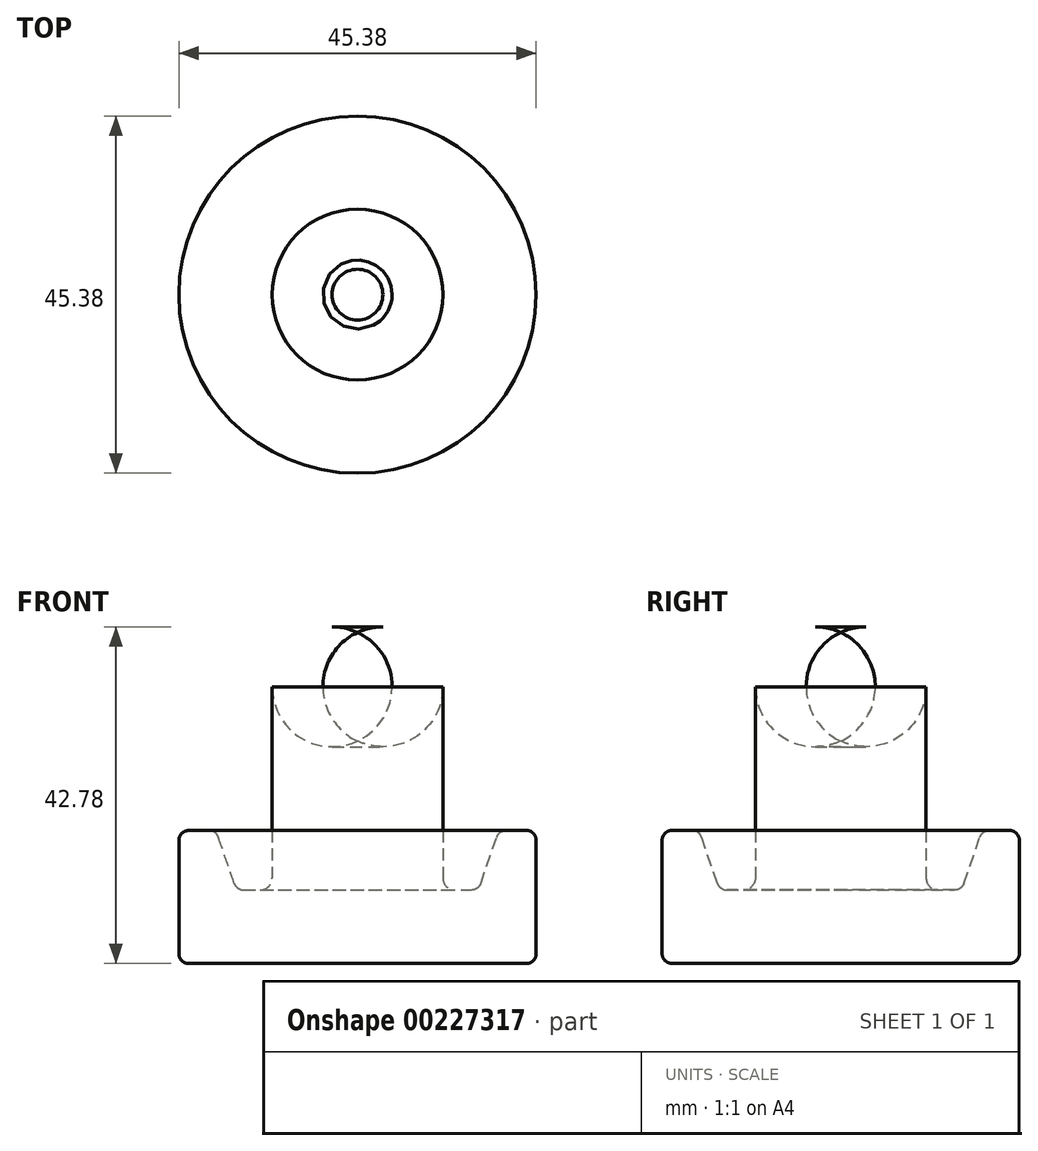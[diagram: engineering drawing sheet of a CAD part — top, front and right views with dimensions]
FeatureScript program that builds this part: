
annotation { "Feature Type Name" : "Feature", "Feature Type Description" : "" }
export const myFeature = defineFeature(function(context is Context, id is Id, definition is map)
    precondition{}
    {
        {
            var Q0;
            Q0=qCreatedBy(makeId("Right.planeOp"),FACE);
            var sketch = newSketch(context, id + "F0", { "sketchPlane" : qUnion([Q0])});
            skLineSegment(sketch, "E0", {"start": v(0, 0) * mm, "end": v(0, 42.78) * mm});
            skLineSegment(sketch, "E1", {"start": v(0, 42.78) * mm, "end": v(-3.23, 42.78) * mm});
            skLineSegment(sketch, "E2", {"start": v(-10.85, 35.16) * mm, "end": v(-10.85, 10.86) * mm});
            skLineSegment(sketch, "E3", {"start": v(-12.37, 9.34) * mm, "end": v(-14.46, 9.34) * mm});
            skLineSegment(sketch, "E4", {"start": v(-15.66, 10.19) * mm, "end": v(-17.67, 16.05) * mm});
            skLineSegment(sketch, "E5", {"start": v(-18.86, 16.9) * mm, "end": v(-21.43, 16.9) * mm});
            skLineSegment(sketch, "E6", {"start": v(-22.7, 15.64) * mm, "end": v(-22.7, 1.26) * mm});
            skLineSegment(sketch, "E7", {"start": v(-21.43, 0) * mm, "end": v(0, 0) * mm});
            skPoint(sketch, "E8.visualSharp", {"position": v(-10.85, 42.78) * mm});
            skArc(sketch, "E8.filletArc", {"start": v(-3.23, 42.78) * mm, "mid": v(-8.62, 40.55) * mm, "end": v(-10.85, 35.16) * mm});
            skPoint(sketch, "E9.visualSharp", {"position": v(-10.85, 9.34) * mm});
            skArc(sketch, "E9.filletArc", {"start": v(-12.37, 9.34) * mm, "mid": v(-11.3, 9.78) * mm, "end": v(-10.85, 10.86) * mm});
            skPoint(sketch, "E10.visualSharp", {"position": v(-15.36, 9.34) * mm});
            skArc(sketch, "E10.filletArc", {"start": v(-15.66, 10.19) * mm, "mid": v(-15.2, 9.57) * mm, "end": v(-14.46, 9.34) * mm});
            skPoint(sketch, "E11.visualSharp", {"position": v(-17.96, 16.9) * mm});
            skArc(sketch, "E11.filletArc", {"start": v(-17.67, 16.05) * mm, "mid": v(-18.13, 16.67) * mm, "end": v(-18.86, 16.9) * mm});
            skPoint(sketch, "E12.visualSharp", {"position": v(-22.7, 16.9) * mm});
            skArc(sketch, "E12.filletArc", {"start": v(-21.43, 16.9) * mm, "mid": v(-22.32, 16.53) * mm, "end": v(-22.7, 15.64) * mm});
            skPoint(sketch, "E13.visualSharp", {"position": v(-22.7, 0) * mm});
            skArc(sketch, "E13.filletArc", {"start": v(-22.7, 1.26) * mm, "mid": v(-22.32, 0.37) * mm, "end": v(-21.43, 0) * mm});
            skSolve(sketch);
        }
        {
            var Q0;
            Q0 = qSketchRegion(id + "F0", true);
            var Q1;
            Q1=sQuery(id+"F0.wireOp",EDGE,"E0");
            revolve(context, id + "F1", {"entities" : qUnion([Q0]), "axis" : qUnion([Q1]), "revolveType" : RevolveType.FULL});
        }
    });
